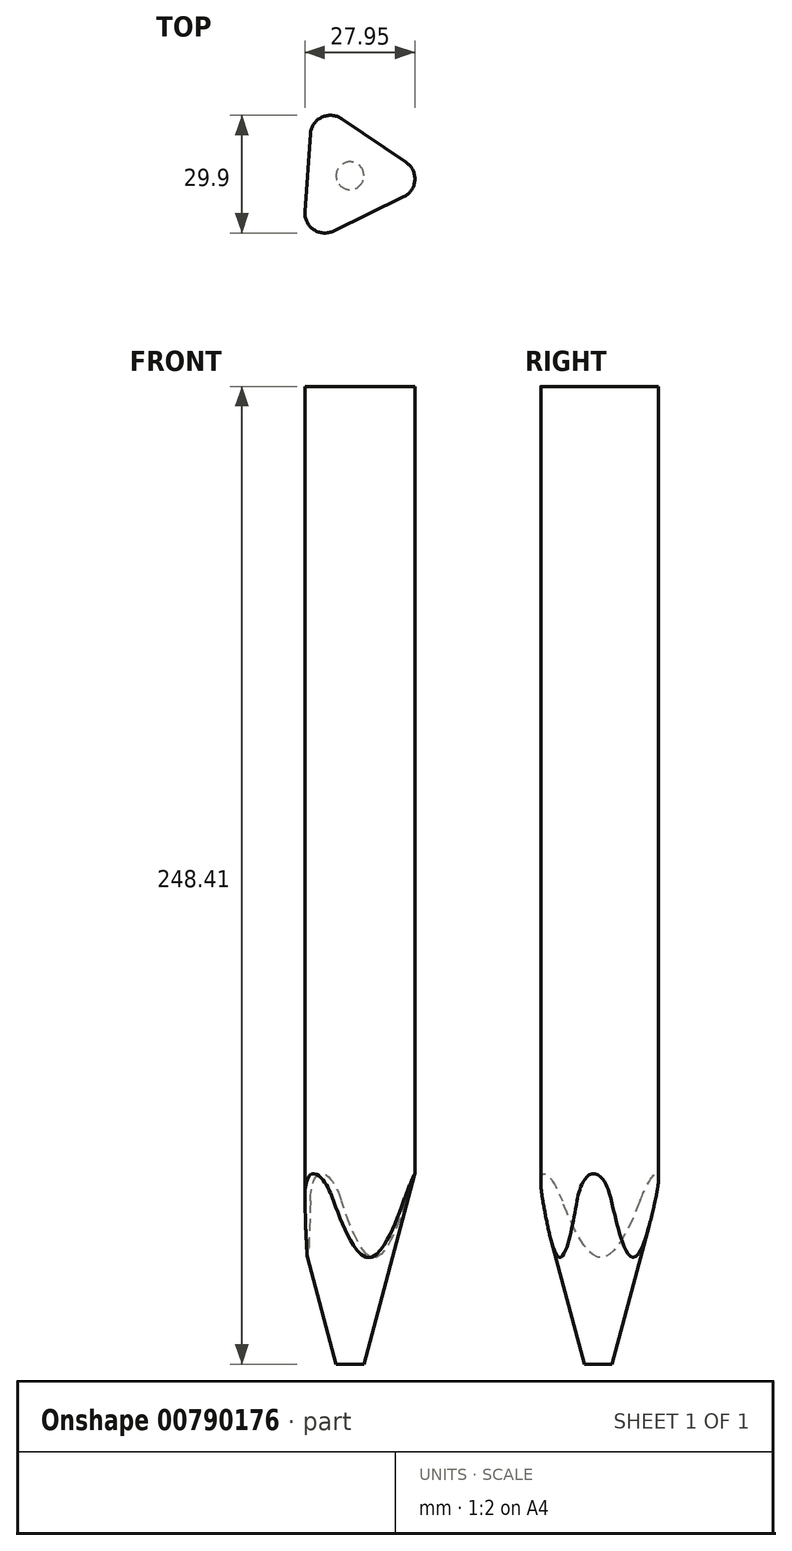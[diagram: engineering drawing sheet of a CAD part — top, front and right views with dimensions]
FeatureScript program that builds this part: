
annotation { "Feature Type Name" : "Feature", "Feature Type Description" : "" }
export const myFeature = defineFeature(function(context is Context, id is Id, definition is map)
    precondition{}
    {
        {
            var Q0;
            Q0=qCreatedBy(makeId("Top.planeOp"),FACE);
            var sketch = newSketch(context, id + "F0", { "sketchPlane" : qUnion([Q0])});
            skCircle(sketch, "E0.cCircle", {"center": v(0, 0) * mm, "radius": 10.8 * mm, "construction": true});
            skLineSegment(sketch, "E0.0", {"start": v(-2.16, 14.48) * mm, "end": v(14.24, 3.4) * mm});
            skLineSegment(sketch, "E0.1", {"start": v(13.62, -5.37) * mm, "end": v(-4.17, -14.03) * mm});
            skLineSegment(sketch, "E0.2", {"start": v(-11.46, -9.11) * mm, "end": v(-10.07, 10.63) * mm});
            skPoint(sketch, "E0.0.midPoint", {"position": v(6.04, 8.94) * mm});
            skPoint(sketch, "E1.visualSharp", {"position": v(-9.45, 19.4) * mm});
            skArc(sketch, "E1.filletArc", {"start": v(-2.16, 14.48) * mm, "mid": v(-7.23, 14.84) * mm, "end": v(-10.07, 10.63) * mm});
            skPoint(sketch, "E2.visualSharp", {"position": v(-12.08, -17.89) * mm});
            skArc(sketch, "E2.filletArc", {"start": v(-11.46, -9.11) * mm, "mid": v(-9.24, -13.68) * mm, "end": v(-4.17, -14.03) * mm});
            skPoint(sketch, "E3.visualSharp", {"position": v(21.53, -1.52) * mm});
            skArc(sketch, "E3.filletArc", {"start": v(13.62, -5.37) * mm, "mid": v(16.46, -1.16) * mm, "end": v(14.24, 3.4) * mm});
            skCircle(sketch, "E4", {"center": v(0, 0) * mm, "radius": 18.84 * mm});
            skSolve(sketch);
        }
        {
            var Q0;
            Q0=makeQuery(id+"F0.imprint","IMPRINT",FACE,{"disambiguationData":[TD([[makeQuery(id+"F0.imprint","IMPRINT",EDGE,{"derivedFrom":sQuery(id+"F0.wireOp",EDGE,"E0.0")}),-1.0]])]});
            var Q1;
            Q1=makeQuery(id+"F0.imprint","IMPRINT",FACE,{"disambiguationData":[TD([[makeQuery(id+"F0.imprint","IMPRINT",EDGE,{"derivedFrom":sQuery(id+"F0.wireOp",EDGE,"E0.0")}),1.0]])]});
            extrude(context, id + "F1", {"entities" : qUnion([Q0, Q1]), "oppositeDirection" : true, "depth" : 74.68 * mm, "offsetDistance" : 25.4 * mm, "hasDraft" : true, "draftAngle" : 15 * degree, "draftPullDirection" : true});
        }
        {
            var Q0;
            Q0=makeQuery(id+"F0.imprint","IMPRINT",FACE,{"disambiguationData":[TD([[makeQuery(id+"F0.imprint","IMPRINT",EDGE,{"derivedFrom":sQuery(id+"F0.wireOp",EDGE,"E0.0")}),-1.0]])]});
            extrude(context, id + "F2", {"entities" : qUnion([Q0]), "operationType" : NewBodyOperationType.INTERSECT, "oppositeDirection" : true, "depth" : 57.15 * mm, "offsetDistance" : 25.4 * mm});
        }
        {
            var Q0;
            Q0=makeQuery(id+"F0.imprint","IMPRINT",FACE,{"disambiguationData":[TD([[makeQuery(id+"F0.imprint","IMPRINT",EDGE,{"derivedFrom":sQuery(id+"F0.wireOp",EDGE,"E0.0")}),-1.0]])]});
            extrude(context, id + "F3", {"entities" : qUnion([Q0]), "operationType" : NewBodyOperationType.ADD, "depth" : 191.26 * mm, "offsetDistance" : 25.4 * mm});
        }
    });
